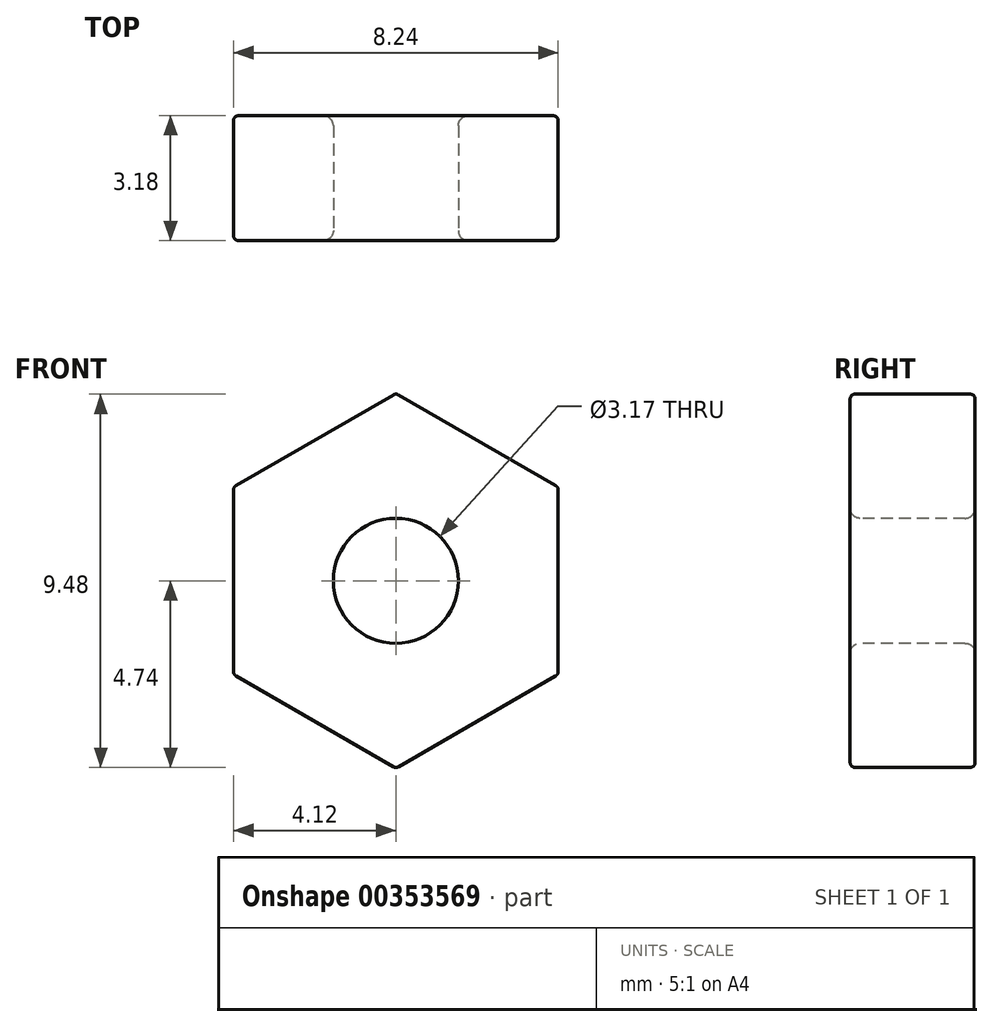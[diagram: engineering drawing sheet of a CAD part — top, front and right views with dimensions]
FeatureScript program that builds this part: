
annotation { "Feature Type Name" : "Feature", "Feature Type Description" : "" }
export const myFeature = defineFeature(function(context is Context, id is Id, definition is map)
    precondition{}
    {
        {
            var Q0;
            Q0=qCreatedBy(makeId("Front.planeOp"),FACE);
            var sketch = newSketch(context, id + "F0", { "sketchPlane" : qUnion([Q0])});
            skCircle(sketch, "E0.cCircle", {"center": v(0, 0) * mm, "radius": 4.12 * mm, "construction": true});
            skLineSegment(sketch, "E0.0", {"start": v(0, 4.76) * mm, "end": v(4.12, 2.38) * mm});
            skLineSegment(sketch, "E0.1", {"start": v(4.12, 2.38) * mm, "end": v(4.12, -2.38) * mm});
            skLineSegment(sketch, "E0.2", {"start": v(4.12, -2.38) * mm, "end": v(0, -4.76) * mm});
            skLineSegment(sketch, "E0.3", {"start": v(0, -4.76) * mm, "end": v(-4.12, -2.38) * mm});
            skLineSegment(sketch, "E0.4", {"start": v(-4.12, -2.38) * mm, "end": v(-4.12, 2.38) * mm});
            skLineSegment(sketch, "E0.5", {"start": v(-4.12, 2.38) * mm, "end": v(0, 4.76) * mm});
            skPoint(sketch, "E0.0.midPoint", {"position": v(2.06, 3.57) * mm});
            skSolve(sketch);
        }
        {
            var Q0;
            Q0 = qSketchRegion(id + "F0", true);
            extrude(context, id + "F1", {"entities" : qUnion([Q0]), "depth" : 3.17 * mm, "symmetric" : true});
        }
        {
            var Q0;
            Q0=makeQuery(id+"F1.opExtrude","CAP_FACE",FACE,{"disambiguationData":[OSD([sQuery(id+"F0.wireOp",EDGE,"E0.0"),sQuery(id+"F0.wireOp",EDGE,"E0.1"),sQuery(id+"F0.wireOp",EDGE,"E0.2"),sQuery(id+"F0.wireOp",EDGE,"E0.3"),sQuery(id+"F0.wireOp",EDGE,"E0.4"),sQuery(id+"F0.wireOp",EDGE,"E0.5")])],"isStart":false});
            var sketch = newSketch(context, id + "F2", { "sketchPlane" : qUnion([Q0])});
            skCircle(sketch, "E1", {"center": v(0, 0) * mm, "radius": 1.59 * mm});
            skSolve(sketch);
        }
        {
            var Q0;
            Q0 = qSketchRegion(id + "F2", true);
            extrude(context, id + "F3", {"entities" : qUnion([Q0]), "operationType" : NewBodyOperationType.REMOVE, "endBound" : BoundingType.THROUGH_ALL, "oppositeDirection" : true, "depth" : 25.4 * mm});
        }
        {
            var Q0;
            Q0=makeQuery(id+"F1.opExtrude","CAP_EDGE",EDGE,{"disambiguationData":[OSD([sQuery(id+"F0.wireOp",EDGE,"E0.5")])],"isStart":false});
            var Q1;
            Q1=makeQuery(id+"F1.opExtrude","CAP_EDGE",EDGE,{"disambiguationData":[OSD([sQuery(id+"F0.wireOp",EDGE,"E0.4")])],"isStart":false});
            var Q2;
            Q2=makeQuery(id+"F1.opExtrude","CAP_EDGE",EDGE,{"disambiguationData":[OSD([sQuery(id+"F0.wireOp",EDGE,"E0.0")])],"isStart":false});
            var Q3;
            Q3=makeQuery(id+"F1.opExtrude","CAP_EDGE",EDGE,{"disambiguationData":[OSD([sQuery(id+"F0.wireOp",EDGE,"E0.3")])],"isStart":false});
            var Q4;
            Q4=makeQuery(id+"F1.opExtrude","CAP_EDGE",EDGE,{"disambiguationData":[OSD([sQuery(id+"F0.wireOp",EDGE,"E0.2")])],"isStart":false});
            var Q5;
            Q5=makeQuery(id+"F1.opExtrude","CAP_EDGE",EDGE,{"disambiguationData":[OSD([sQuery(id+"F0.wireOp",EDGE,"E0.1")])],"isStart":false});
            var Q6;
            Q6=makeQuery(id+"F1.opExtrude","SWEPT_EDGE",EDGE,{"disambiguationData":[OSD([sQuery(id+"F0.wireOp",EDGE,"E0.0"),sQuery(id+"F0.wireOp",EDGE,"E0.1")])]});
            var Q7;
            Q7=makeQuery(id+"F1.opExtrude","SWEPT_EDGE",EDGE,{"disambiguationData":[OSD([sQuery(id+"F0.wireOp",EDGE,"E0.0"),sQuery(id+"F0.wireOp",EDGE,"E0.5")])]});
            var Q8;
            Q8=makeQuery(id+"F1.opExtrude","CAP_EDGE",EDGE,{"disambiguationData":[OSD([sQuery(id+"F0.wireOp",EDGE,"E0.1")])],"isStart":true});
            var Q9;
            Q9=makeQuery(id+"F1.opExtrude","CAP_EDGE",EDGE,{"disambiguationData":[OSD([sQuery(id+"F0.wireOp",EDGE,"E0.0")])],"isStart":true});
            var Q10;
            Q10=makeQuery(id+"F1.opExtrude","CAP_EDGE",EDGE,{"disambiguationData":[OSD([sQuery(id+"F0.wireOp",EDGE,"E0.4")])],"isStart":true});
            var Q11;
            Q11=makeQuery(id+"F1.opExtrude","CAP_EDGE",EDGE,{"disambiguationData":[OSD([sQuery(id+"F0.wireOp",EDGE,"E0.5")])],"isStart":true});
            var Q12;
            Q12=makeQuery(id+"F1.opExtrude","CAP_EDGE",EDGE,{"disambiguationData":[OSD([sQuery(id+"F0.wireOp",EDGE,"E0.2")])],"isStart":true});
            var Q13;
            Q13=makeQuery(id+"F1.opExtrude","SWEPT_EDGE",EDGE,{"disambiguationData":[OSD([sQuery(id+"F0.wireOp",EDGE,"E0.1"),sQuery(id+"F0.wireOp",EDGE,"E0.2")])]});
            var Q14;
            Q14=makeQuery(id+"F1.opExtrude","CAP_EDGE",EDGE,{"disambiguationData":[OSD([sQuery(id+"F0.wireOp",EDGE,"E0.3")])],"isStart":true});
            var Q15;
            Q15=makeQuery(id+"F1.opExtrude","SWEPT_EDGE",EDGE,{"disambiguationData":[OSD([sQuery(id+"F0.wireOp",EDGE,"E0.2"),sQuery(id+"F0.wireOp",EDGE,"E0.3")])]});
            var Q16;
            Q16=makeQuery(id+"F1.opExtrude","SWEPT_EDGE",EDGE,{"disambiguationData":[OSD([sQuery(id+"F0.wireOp",EDGE,"E0.3"),sQuery(id+"F0.wireOp",EDGE,"E0.4")])]});
            var Q17;
            Q17=makeQuery(id+"F1.opExtrude","SWEPT_EDGE",EDGE,{"disambiguationData":[OSD([sQuery(id+"F0.wireOp",EDGE,"E0.4"),sQuery(id+"F0.wireOp",EDGE,"E0.5")])]});
            fillet(context, id + "F4", {"entities" : qUnion([Q0, Q1, Q2, Q3, Q4, Q5, Q6, Q7, Q8, Q9, Q10, Q11, Q12, Q13, Q14, Q15, Q16, Q17]), "radius" : 0.13 * mm, "tangentPropagation" : true, "allowEdgeOverflow" : false});
        }
        {
            var Q0;
            Q0=makeQuery(id+"F1.opExtrude","CAP_FACE",FACE,{"disambiguationData":[OSD([sQuery(id+"F0.wireOp",EDGE,"E0.0"),sQuery(id+"F0.wireOp",EDGE,"E0.1"),sQuery(id+"F0.wireOp",EDGE,"E0.2"),sQuery(id+"F0.wireOp",EDGE,"E0.3"),sQuery(id+"F0.wireOp",EDGE,"E0.4"),sQuery(id+"F0.wireOp",EDGE,"E0.5")])],"isStart":false});
            var Q1;
            Q1=makeQuery(id+"F3.boolean.opBoolean","COPY",FACE,{"derivedFrom":makeQuery(id+"F3.opExtrude","SWEPT_FACE",FACE,{"disambiguationData":[OSD([sQuery(id+"F2.wireOp",EDGE,"E1")])]})});
            fillet(context, id + "F5", {"entities" : qUnion([Q0, Q1]), "radius" : 0.25 * mm, "tangentPropagation" : true, "allowEdgeOverflow" : false});
        }
    });
